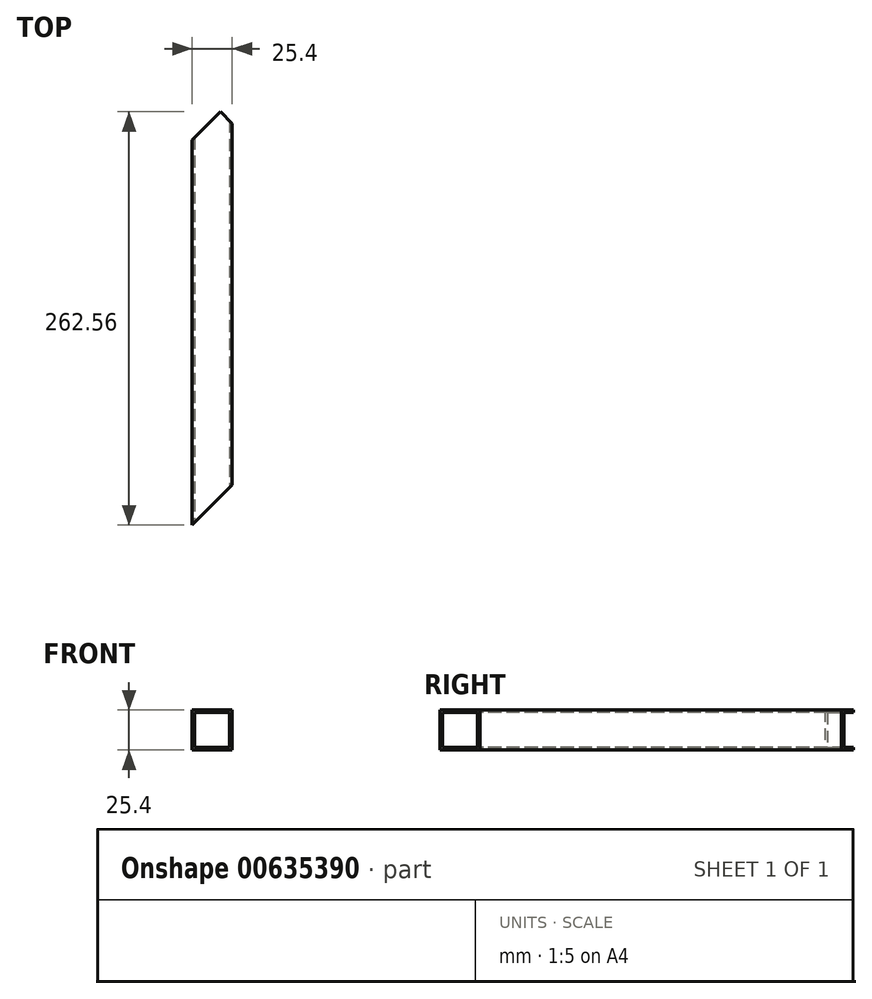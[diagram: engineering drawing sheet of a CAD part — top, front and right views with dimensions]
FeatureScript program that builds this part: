
annotation { "Feature Type Name" : "Feature", "Feature Type Description" : "" }
export const myFeature = defineFeature(function(context is Context, id is Id, definition is map)
    precondition{}
    {
        {
            var Q0;
            Q0=qCreatedBy(makeId("Top.planeOp"),FACE);
            var sketch = newSketch(context, id + "F0", { "sketchPlane" : qUnion([Q0])});
            skLineSegment(sketch, "E0.bottom", {"start": v(-12.7, 135) * mm, "end": v(12.7, 135) * mm});
            skLineSegment(sketch, "E0.top", {"start": v(-12.7, -135) * mm, "end": v(12.7, -135) * mm});
            skLineSegment(sketch, "E0.left", {"start": v(-12.7, 135) * mm, "end": v(-12.7, -135) * mm});
            skLineSegment(sketch, "E0.right", {"start": v(12.7, 135) * mm, "end": v(12.7, -135) * mm});
            skPoint(sketch, "E0.middle", {"position": v(0, 0) * mm});
            skLineSegment(sketch, "E1", {"start": v(12.7, 135) * mm, "end": v(-12.7, 109.6) * mm});
            skPoint(sketch, "E2", {"position": v(5.26, 127.56) * mm});
            skLineSegment(sketch, "E3", {"start": v(5.26, 127.56) * mm, "end": v(12.7, 120.12) * mm});
            skSolve(sketch);
        }
        {
            var Q0;
            {var subQ0=sQuery(id+"F0.wireOp",EDGE,"E3");Q0=makeQuery(id+"F0.imprint","IMPRINT",FACE,{"disambiguationData":[TD([[makeQuery(id+"F0.imprint","IMPRINT",EDGE,{"derivedFrom":subQ0}),-1.0]])]});}
            extrude(context, id + "F1", {"entities" : qUnion([Q0]), "depth" : 25.4 * mm});
        }
        {
            var Q0;
            Q0=makeQuery(id+"F1.opExtrude","SWEPT_FACE",FACE,{"disambiguationData":[OSD([sQuery(id+"F0.wireOp",EDGE,"E0.top")])]});
            shell(context, id + "F2", {"entities" : qUnion([Q0]), "thickness" : 1.59 * mm});
        }
        {
            var Q0;
            Q0=makeQuery(id+"F1.opExtrude","SWEPT_FACE",FACE,{"disambiguationData":[OSD([sQuery(id+"F0.wireOp",EDGE,"E0.top")])]});
            var sketch = newSketch(context, id + "F3", { "sketchPlane" : qUnion([Q0])});
            skLineSegment(sketch, "E4.bottom", {"start": v(-11.11, 23.81) * mm, "end": v(11.11, 23.81) * mm});
            skLineSegment(sketch, "E4.top", {"start": v(-11.11, 1.59) * mm, "end": v(11.11, 1.59) * mm});
            skLineSegment(sketch, "E4.left", {"start": v(-11.11, 23.81) * mm, "end": v(-11.11, 1.59) * mm});
            skLineSegment(sketch, "E4.right", {"start": v(11.11, 23.81) * mm, "end": v(11.11, 1.59) * mm});
            skSolve(sketch);
        }
        {
            var Q0;
            Q0=qSketchRegion(id+"F3",true);
            extrude(context, id + "F4", {"entities" : qUnion([Q0]), "operationType" : NewBodyOperationType.REMOVE, "endBound" : BoundingType.THROUGH_ALL, "oppositeDirection" : true, "depth" : 25.4 * mm});
        }
        {
            var Q0;
            Q0=makeQuery(id+"F1.opExtrude","CAP_FACE",FACE,{"disambiguationData":[OSD([sQuery(id+"F0.wireOp",EDGE,"E0.top"),sQuery(id+"F0.wireOp",EDGE,"E0.left"),sQuery(id+"F0.wireOp",EDGE,"E0.right"),sQuery(id+"F0.wireOp",EDGE,"E1"),sQuery(id+"F0.wireOp",EDGE,"E3")])],"isStart":false});
            var sketch = newSketch(context, id + "F5", { "sketchPlane" : qUnion([Q0])});
            skLineSegment(sketch, "E5", {"start": v(-12.7, -135) * mm, "end": v(12.7, -109.6) * mm});
            skSolve(sketch);
        }
        {
            var Q0;
            {var subQ0=sQuery(id+"F5.wireOp",EDGE,"E5");Q0=makeQuery(id+"F5.imprint","IMPRINT",FACE,{"disambiguationData":[TD([[makeQuery(id+"F5.imprint","IMPRINT",EDGE,{"derivedFrom":subQ0}),-1.0]])]});}
            extrude(context, id + "F6", {"entities" : qUnion([Q0]), "operationType" : NewBodyOperationType.REMOVE, "oppositeDirection" : true, "depth" : 25.4 * mm});
        }
    });
